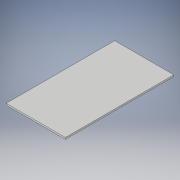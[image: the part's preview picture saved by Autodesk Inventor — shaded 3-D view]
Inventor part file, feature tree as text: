
AUTODESK INVENTOR PART (.ipt)
format: ipt  version: 2017 (Build 210142000, 142)  size: 89,600 bytes
history: native  units: in
note: dims shown in document units (in); Inventor stores cm internally (conversion verified against a paired STEP export)
features: extrude x1, sketch x1
ambient origin geometry x8: Origin, YZ Plane, XZ Plane, XY Plane, X Axis, Y Axis, Z Axis, Center Point
bodies: Solid1 (feature_tree)
feature tree (2):
  extrude  "Extrusion1"  Depth=66.0in
  sketch  "Sketch1"  dims[d0=36.0in d1=66.0in d2=1.0in d3=0.0in]
